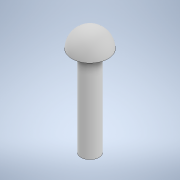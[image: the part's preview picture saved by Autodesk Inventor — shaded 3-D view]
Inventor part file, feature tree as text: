
AUTODESK INVENTOR PART (.ipt)
format: ipt  version: 2022 (Build 260153000, 153)  size: 112,640 bytes
history: native  units: in
note: dims shown in document units (in); Inventor stores cm internally (conversion verified against a paired STEP export)
features: extrude x2, sketch x2, fillet x1
ambient origin geometry x8: Origin, YZ Plane, XZ Plane, XY Plane, X Axis, Y Axis, Z Axis, Center Point
bodies: Solid1 (feature_tree)
feature tree (5):
  extrude  "Extrusion1"  Depth=0.5906in TaperAngle=0.0deg
  extrude  "Extrusion2"  Depth=0.1181in TaperAngle=0.0deg
  fillet  "Fillet1"  Radius=0.1181in
  sketch  "Sketch1"  dims[d0=0.1181in d1=0.5906in d2=0.0in]
  sketch  "Sketch2"  dims[d3=0.2362in d4=0.1181in d5=0.0in d6=0.1181in d7=0.0344in]
